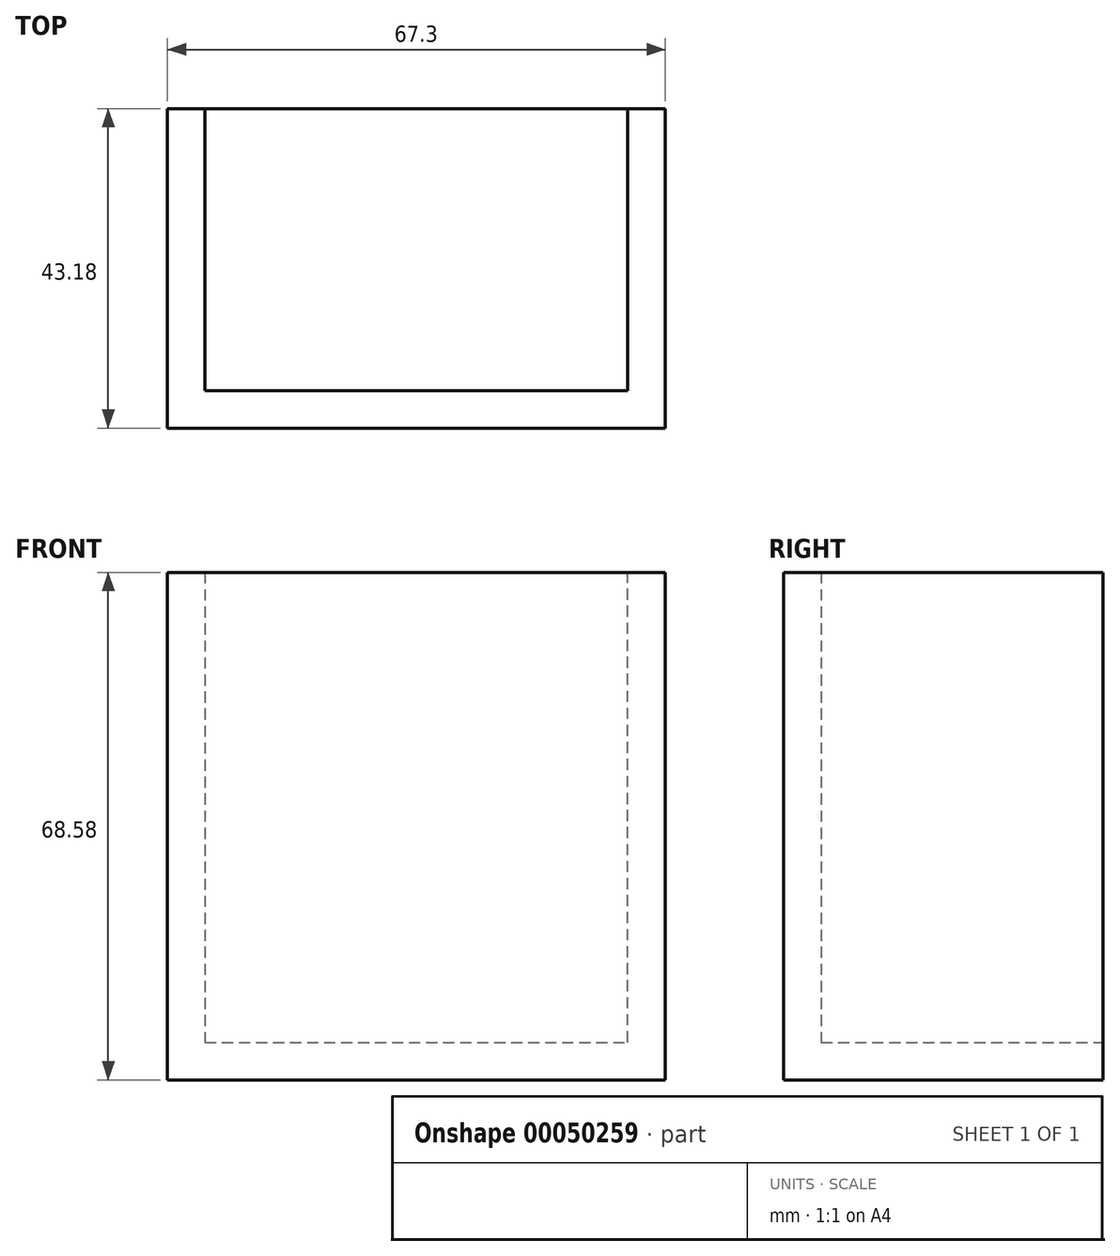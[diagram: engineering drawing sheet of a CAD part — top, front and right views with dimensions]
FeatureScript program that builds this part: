
annotation { "Feature Type Name" : "Feature", "Feature Type Description" : "" }
export const myFeature = defineFeature(function(context is Context, id is Id, definition is map)
    precondition{}
    {
        {
            var Q0;
            Q0=qCreatedBy(makeId("Front.planeOp"),FACE);
            var sketch = newSketch(context, id + "F0", { "sketchPlane" : qUnion([Q0])});
            skLineSegment(sketch, "E0", {"start": v(-28.58, 33.02) * mm, "end": v(-28.57, -30.48) * mm});
            skLineSegment(sketch, "E1", {"start": v(-28.57, -30.48) * mm, "end": v(28.58, -30.48) * mm});
            skLineSegment(sketch, "E2", {"start": v(28.58, -30.48) * mm, "end": v(28.57, 33.02) * mm});
            skLineSegment(sketch, "E3", {"start": v(28.57, 33.02) * mm, "end": v(33.65, 33.02) * mm});
            skLineSegment(sketch, "E4", {"start": v(33.65, 33.02) * mm, "end": v(33.65, -35.56) * mm});
            skLineSegment(sketch, "E5", {"start": v(33.66, -35.56) * mm, "end": v(-33.65, -35.56) * mm});
            skLineSegment(sketch, "E6", {"start": v(-33.65, -35.56) * mm, "end": v(-33.66, 33.02) * mm});
            skLineSegment(sketch, "E7", {"start": v(-33.66, 33.02) * mm, "end": v(-28.58, 33.02) * mm});
            skSolve(sketch);
        }
        {
            var Q0;
            Q0=makeQuery(id+"F0.imprint","IMPRINT",FACE,{"disambiguationData":[TD([[makeQuery(id+"F0.imprint","IMPRINT",EDGE,{"derivedFrom":sQuery(id+"F0.wireOp",EDGE,"E0")}),-1.0]])]});
            extrude(context, id + "F1", {"entities" : qUnion([Q0]), "depth" : 38.1 * mm});
        }
        {
            var Q0;
            Q0=makeQuery(id+"F1.opExtrude","CAP_FACE",FACE,{"disambiguationData":[OSD([sQuery(id+"F0.wireOp",EDGE,"E0"),sQuery(id+"F0.wireOp",EDGE,"E1"),sQuery(id+"F0.wireOp",EDGE,"E2"),sQuery(id+"F0.wireOp",EDGE,"E3"),sQuery(id+"F0.wireOp",EDGE,"E4"),sQuery(id+"F0.wireOp",EDGE,"E5"),sQuery(id+"F0.wireOp",EDGE,"E6"),sQuery(id+"F0.wireOp",EDGE,"E7")])],"isStart":false});
            var sketch = newSketch(context, id + "F2", { "sketchPlane" : qUnion([Q0])});
            skLineSegment(sketch, "E8.bottom", {"start": v(-33.66, 33.02) * mm, "end": v(33.66, 33.02) * mm});
            skLineSegment(sketch, "E8.top", {"start": v(-33.66, -35.56) * mm, "end": v(33.66, -35.56) * mm});
            skLineSegment(sketch, "E8.left", {"start": v(-33.66, 33.02) * mm, "end": v(-33.66, -35.56) * mm});
            skLineSegment(sketch, "E8.right", {"start": v(33.66, 33.02) * mm, "end": v(33.66, -35.56) * mm});
            skSolve(sketch);
        }
        {
            var Q0;
            Q0 = qSketchRegion(id + "F2", true);
            extrude(context, id + "F3", {"entities" : qUnion([Q0]), "operationType" : NewBodyOperationType.ADD, "depth" : 5.08 * mm});
        }
    });
